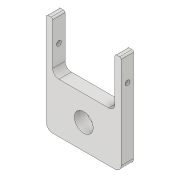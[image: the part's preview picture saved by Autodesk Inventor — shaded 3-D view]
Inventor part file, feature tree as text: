
AUTODESK INVENTOR PART (.ipt)
format: ipt  version: 2018.3 (Build 223284000, 284)  size: 126,464 bytes
history: native  units: in
note: dims shown in document units (in); Inventor stores cm internally (conversion verified against a paired STEP export)
features: extrude x2, fillet x2, sketch x1
ambient origin geometry x8: Origin, YZ Plane, XZ Plane, XY Plane, X Axis, Y Axis, Z Axis, Center Point
bodies: Solid1 (feature_tree)
feature tree (5):
  extrude  "Extrusion1"  Depth=2.0in
  extrude  "Extrusion9"  Depth=2.0in
  fillet  "Fillet13"  Radius=0.5in
  fillet  "Fillet14"  Radius=1.0in
  sketch  "Sketch9"  dims[d0=0.755in d1=2.0in d2=2.0in d3=0.5in d4=0.0in d37=1.0in d44=4.0in d45=4.0in d48=0.1925in d49=0.25in d50=1.0in d51=1.0in d52=0.0in d53=0.0625in d54=0.25in d23=1.0in d24=1.0in]
